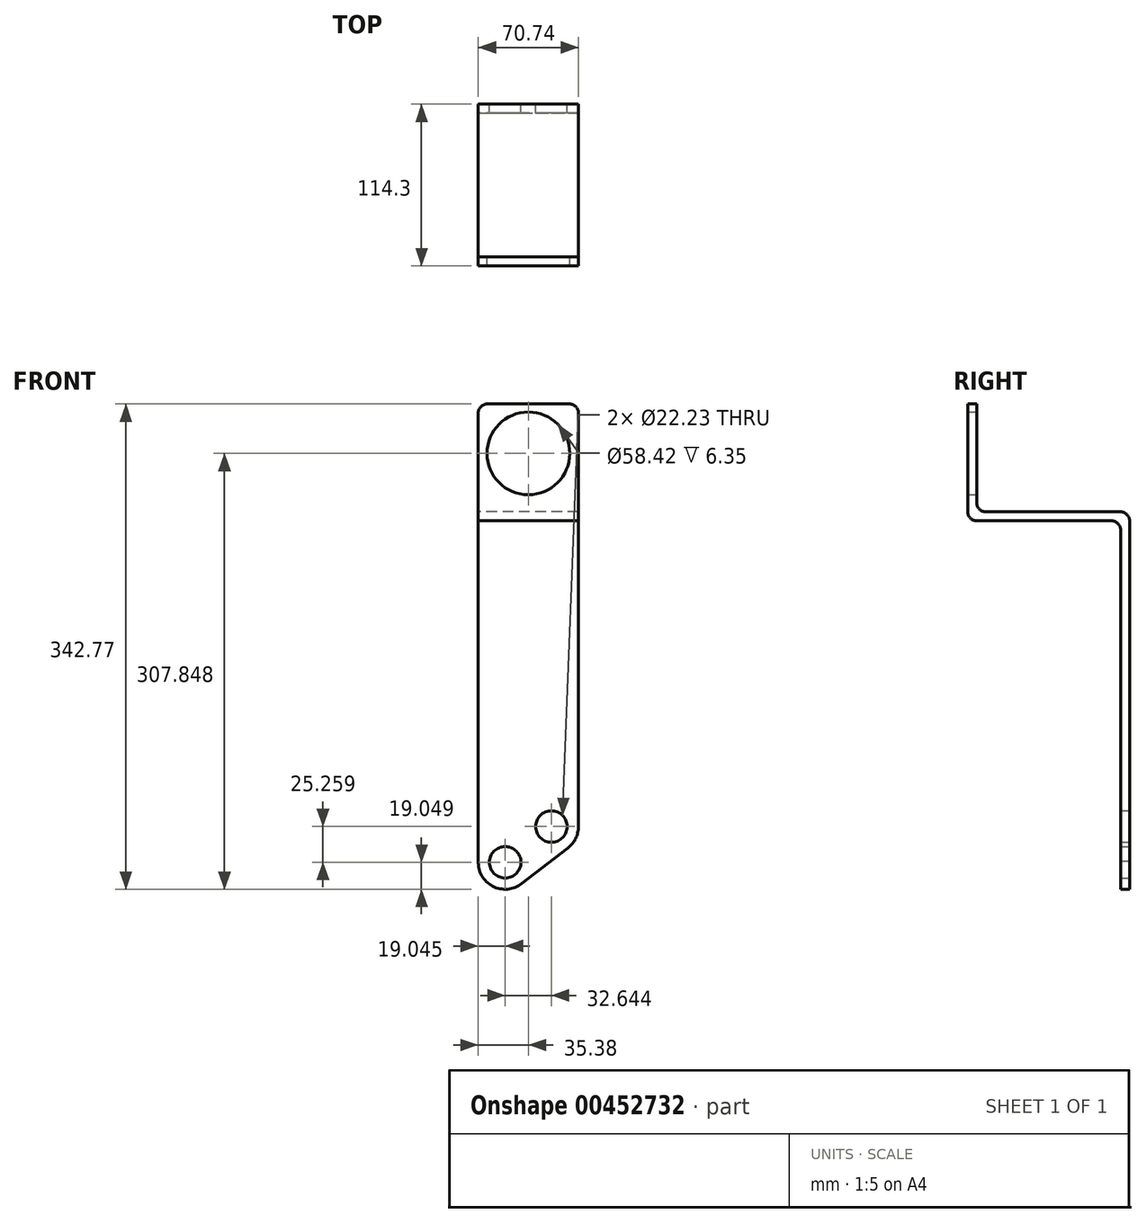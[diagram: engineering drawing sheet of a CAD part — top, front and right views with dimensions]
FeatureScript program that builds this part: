
annotation { "Feature Type Name" : "Feature", "Feature Type Description" : "" }
export const myFeature = defineFeature(function(context is Context, id is Id, definition is map)
    precondition{}
    {
        {
            var Q0;
            Q0=qCreatedBy(makeId("Front.planeOp"),FACE);
            var sketch = newSketch(context, id + "F0", { "sketchPlane" : qUnion([Q0])});
            skCircle(sketch, "E0", {"center": v(0, 0) * mm, "radius": 228.6 * mm, "construction": true});
            skCircle(sketch, "E1", {"center": v(-155.64, 167.43) * mm, "radius": 11.11 * mm});
            skCircle(sketch, "E2", {"center": v(-123, 192.69) * mm, "radius": 11.11 * mm});
            skLineSegment(sketch, "E3", {"start": v(0, 0) * mm, "end": v(0, 228.6) * mm});
            skArc(sketch, "E4", {"start": v(-174.67, 168.41) * mm, "mid": v(-164.47, 150.55) * mm, "end": v(-143.99, 152.36) * mm});
            skArc(sketch, "E5", {"start": v(-111.34, 177.62) * mm, "mid": v(-105.9, 184.3) * mm, "end": v(-103.95, 192.69) * mm});
            skLineSegment(sketch, "E6", {"start": v(-143.99, 152.36) * mm, "end": v(-111.34, 177.62) * mm});
            skLineSegment(sketch, "E7", {"start": v(-174.67, 168.41) * mm, "end": v(-174.67, 281.6) * mm});
            skLineSegment(sketch, "E8", {"start": v(-174.67, 281.6) * mm, "end": v(-103.95, 281.6) * mm});
            skLineSegment(sketch, "E9", {"start": v(-103.95, 281.6) * mm, "end": v(-103.95, 192.69) * mm});
            skSolve(sketch);
        }
        {
            var Q0;
            Q0 = qSketchRegion(id + "F0", true);
            extrude(context, id + "F1", {"entities" : qUnion([Q0]), "depth" : 6.35 * mm});
        }
        {
            var Q0;
            Q0=makeQuery(id+"F1.opExtrude","SWEPT_FACE",FACE,{"disambiguationData":[OSD([sQuery(id+"F0.wireOp",EDGE,"E7")])]});
            var sketch = newSketch(context, id + "F2", { "sketchPlane" : qUnion([Q0])});
            skLineSegment(sketch, "E10", {"start": v(0, 281.6) * mm, "end": v(0, 408.6) * mm});
            skLineSegment(sketch, "E11", {"start": v(6.35, 414.95) * mm, "end": v(101.6, 414.95) * mm});
            skLineSegment(sketch, "E12", {"start": v(107.95, 421.3) * mm, "end": v(107.95, 491.15) * mm});
            skLineSegment(sketch, "E13", {"start": v(107.95, 491.15) * mm, "end": v(114.3, 491.15) * mm});
            skLineSegment(sketch, "E14", {"start": v(114.3, 491.15) * mm, "end": v(114.3, 414.95) * mm});
            skLineSegment(sketch, "E15", {"start": v(107.95, 408.6) * mm, "end": v(12.7, 408.6) * mm});
            skLineSegment(sketch, "E16", {"start": v(6.35, 402.25) * mm, "end": v(6.35, 281.6) * mm});
            skLineSegment(sketch, "E17", {"start": v(0, 281.6) * mm, "end": v(6.35, 281.6) * mm});
            skPoint(sketch, "E18.visualSharp", {"position": v(0, 414.95) * mm});
            skArc(sketch, "E18.filletArc", {"start": v(6.35, 414.95) * mm, "mid": v(1.86, 413.1) * mm, "end": v(0, 408.6) * mm});
            skArc(sketch, "E19.filletArc", {"start": v(12.7, 408.6) * mm, "mid": v(8.2, 406.74) * mm, "end": v(6.35, 402.25) * mm});
            skPoint(sketch, "E20.visualSharp", {"position": v(107.95, 414.95) * mm});
            skArc(sketch, "E20.filletArc", {"start": v(101.6, 414.95) * mm, "mid": v(106.1, 416.81) * mm, "end": v(107.95, 421.3) * mm});
            skPoint(sketch, "E21.visualSharp", {"position": v(114.3, 408.6) * mm});
            skArc(sketch, "E21.filletArc", {"start": v(107.95, 408.6) * mm, "mid": v(112.44, 410.46) * mm, "end": v(114.3, 414.95) * mm});
            skSolve(sketch);
        }
        {
            var Q0;
            Q0 = qSketchRegion(id + "F2", true);
            var Q1;
            Q1=makeQuery(id+"F1.opExtrude","SWEPT_FACE",FACE,{"disambiguationData":[OSD([sQuery(id+"F0.wireOp",EDGE,"E9")])]});
            extrude(context, id + "F3", {"entities" : qUnion([Q0]), "operationType" : NewBodyOperationType.ADD, "endBound" : BoundingType.UP_TO_SURFACE, "oppositeDirection" : true, "endBoundEntityFace" : qUnion([Q1]), "depth" : 25.4 * mm});
        }
        {
            var Q0;
            Q0=makeQuery(id+"F3.opExtrude","SWEPT_FACE",FACE,{"disambiguationData":[OSD([sQuery(id+"F2.wireOp",EDGE,"E12")])]});
            var sketch = newSketch(context, id + "F4", { "sketchPlane" : qUnion([Q0])});
            skLineSegment(sketch, "E22", {"start": v(139.31, 491.15) * mm, "end": v(139.31, 456.23) * mm});
            skPoint(sketch, "E22.endSnap0", {"position": v(139.31, 491.15) * mm});
            skCircle(sketch, "E23", {"center": v(139.31, 456.23) * mm, "radius": 29.21 * mm});
            skSolve(sketch);
        }
        {
            var Q0;
            Q0 = qSketchRegion(id + "F4", true);
            var Q1;
            Q1=makeQuery(id+"F3.opExtrude","SWEPT_FACE",FACE,{"disambiguationData":[OSD([sQuery(id+"F2.wireOp",EDGE,"E14")])]});
            extrude(context, id + "F5", {"entities" : qUnion([Q0]), "operationType" : NewBodyOperationType.REMOVE, "endBound" : BoundingType.UP_TO_SURFACE, "oppositeDirection" : true, "endBoundEntityFace" : qUnion([Q1]), "depth" : 25.4 * mm});
        }
        {
            var Q0;
            Q0=makeQuery(id+"F3.opExtrude","SWEPT_FACE",FACE,{"disambiguationData":[OSD([sQuery(id+"F2.wireOp",EDGE,"E12")])]});
            var sketch = newSketch(context, id + "F6", { "sketchPlane" : qUnion([Q0])});
            skLineSegment(sketch, "E24.0", {"start": v(110.3, 491.15) * mm, "end": v(168.32, 491.15) * mm});
            skLineSegment(sketch, "E25.0", {"start": v(103.95, 421.3) * mm, "end": v(103.95, 484.8) * mm});
            skLineSegment(sketch, "E26.0", {"start": v(174.67, 421.3) * mm, "end": v(174.67, 484.8) * mm});
            skPoint(sketch, "E27.visualSharp", {"position": v(103.95, 491.15) * mm});
            skArc(sketch, "E27.filletArc", {"start": v(110.3, 491.15) * mm, "mid": v(105.81, 489.3) * mm, "end": v(103.95, 484.8) * mm});
            skPoint(sketch, "E28.visualSharp", {"position": v(174.67, 491.15) * mm});
            skArc(sketch, "E28.filletArc", {"start": v(174.67, 484.8) * mm, "mid": v(172.8, 489.3) * mm, "end": v(168.32, 491.15) * mm});
            skSolve(sketch);
        }
        {
            var Q0;
            Q0 = qSketchRegion(id + "F6", true);
            var Q1;
            {var subQ0=sQuery(id+"F6.wireOp",EDGE,"E27.filletArc");Q1=makeQuery(id+"F6.imprint","IMPRINT",FACE,{"disambiguationData":[TD([[makeQuery(id+"F6.imprint","IMPRINT",EDGE,{"derivedFrom":subQ0}),-1.0]])]});}
            var Q2;
            {var subQ0=sQuery(id+"F6.wireOp",EDGE,"E28.filletArc");Q2=makeQuery(id+"F6.imprint","IMPRINT",FACE,{"disambiguationData":[TD([[makeQuery(id+"F6.imprint","IMPRINT",EDGE,{"derivedFrom":subQ0}),-1.0]])]});}
            var Q3;
            Q3=makeQuery(id+"F3.opExtrude","SWEPT_FACE",FACE,{"disambiguationData":[OSD([sQuery(id+"F2.wireOp",EDGE,"E14")])]});
            extrude(context, id + "F7", {"entities" : qUnion([Q0, Q1, Q2]), "operationType" : NewBodyOperationType.REMOVE, "endBound" : BoundingType.UP_TO_SURFACE, "oppositeDirection" : true, "endBoundEntityFace" : qUnion([Q3]), "depth" : 25.4 * mm});
        }
    });
